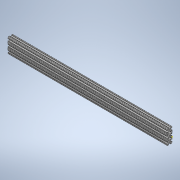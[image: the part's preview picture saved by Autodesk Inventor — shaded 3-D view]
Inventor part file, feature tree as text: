
AUTODESK INVENTOR PART (.ipt)
format: ipt  version: 2020 (Build 240168000, 168)  size: 391,168 bytes
history: native  units: in
note: dims shown in document units (in); Inventor stores cm internally (conversion verified against a paired STEP export)
features: sketch x2, extrude x1
ambient origin geometry x8: Origin, YZ Plane, XZ Plane, XY Plane, X Axis, Y Axis, Z Axis, Center Point
bodies: Solid1 (feature_tree)
feature tree (3):
  extrude  "Extrusion1"  [1 undecoded]
  sketch  "Sketch2"
  sketch  "Sketch1"  dims[d0=32.0in d1=0.0in]
note: 1 required parameter value undecoded (feature->parameter linkage not recoverable at this tier; creation-order binding heuristic only, values carry confidence <= 0.55)
